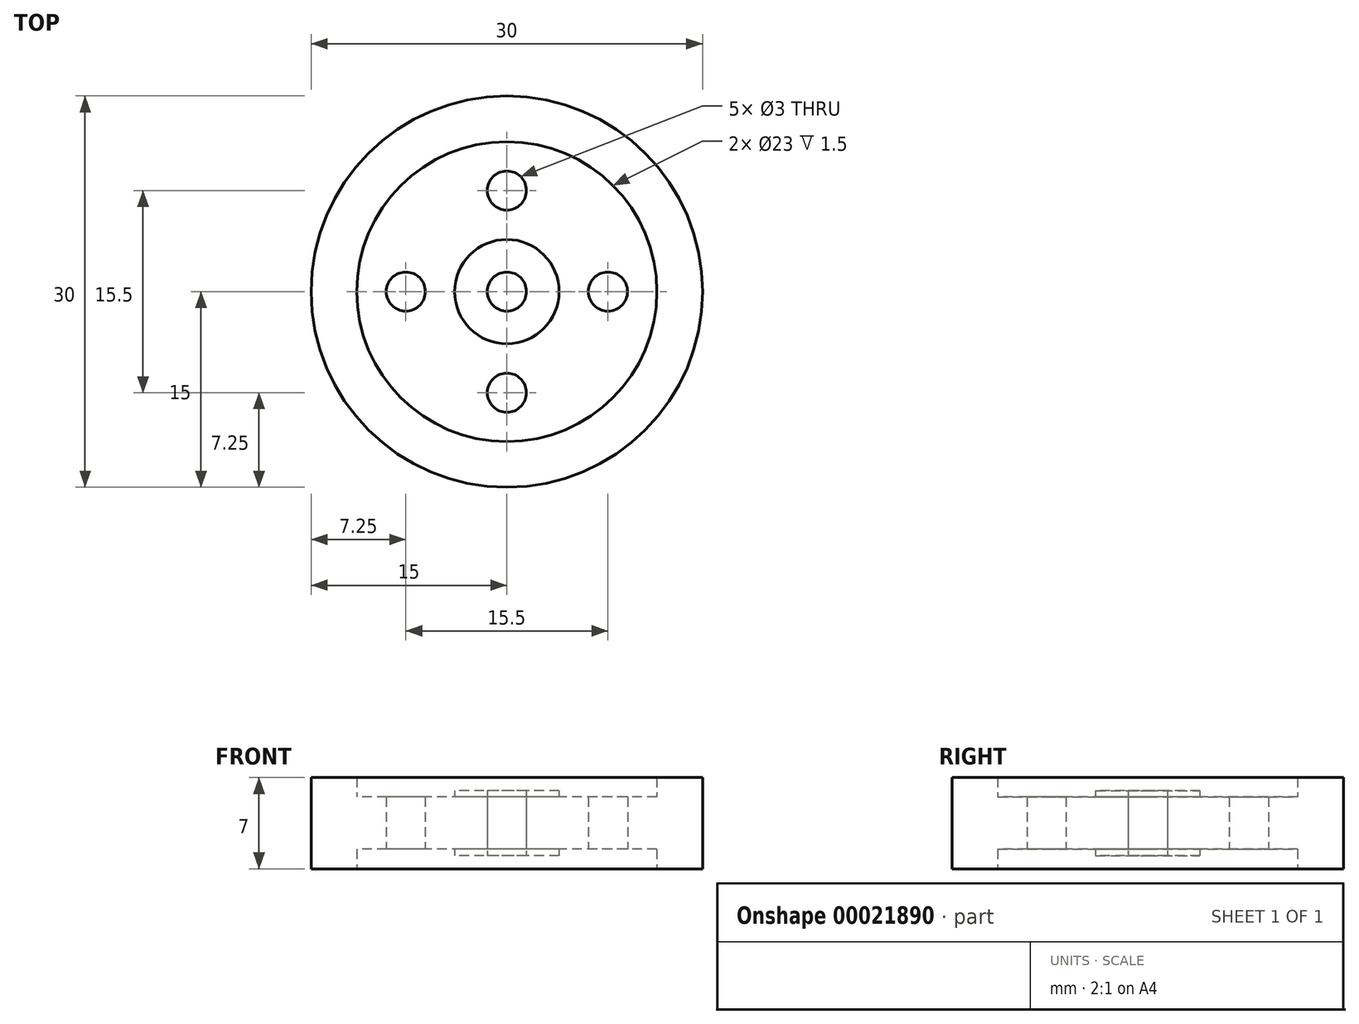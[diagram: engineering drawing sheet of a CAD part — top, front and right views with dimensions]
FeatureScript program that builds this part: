
annotation { "Feature Type Name" : "Feature", "Feature Type Description" : "" }
export const myFeature = defineFeature(function(context is Context, id is Id, definition is map)
    precondition{}
    {
        {
            var Q0;
            Q0=qCreatedBy(makeId("Top.planeOp"),FACE);
            var sketch = newSketch(context, id + "F0", { "sketchPlane" : qUnion([Q0])});
            skCircle(sketch, "E0", {"center": v(0, 0) * mm, "radius": 15 * mm});
            skCircle(sketch, "E1", {"center": v(0, 0) * mm, "radius": 11.5 * mm});
            skCircle(sketch, "E2", {"center": v(0, 0) * mm, "radius": 4 * mm});
            skCircle(sketch, "E3", {"center": v(0, 0) * mm, "radius": 1.5 * mm});
            skLineSegment(sketch, "E4", {"start": v(0, 4) * mm, "end": v(0, 11.5) * mm});
            skLineSegment(sketch, "E5", {"start": v(0, 4) * mm, "end": v(0, 7.75) * mm});
            skCircle(sketch, "E6", {"center": v(0, 7.75) * mm, "radius": 1.5 * mm});
            skCircle(sketch, "E7.1.0", {"center": v(-7.75, 0) * mm, "radius": 1.5 * mm});
            skCircle(sketch, "E7.2.0", {"center": v(0, -7.75) * mm, "radius": 1.5 * mm});
            skCircle(sketch, "E7.3.0", {"center": v(7.75, 0) * mm, "radius": 1.5 * mm});
            skSolve(sketch);
        }
        {
            var Q0;
            Q0=makeQuery(id+"F0.imprint","IMPRINT",FACE,{"disambiguationData":[TD([[makeQuery(id+"F0.imprint","IMPRINT",EDGE,{"derivedFrom":sQuery(id+"F0.wireOp",EDGE,"E0")}),1.0]])]});
            extrude(context, id + "F1", {"entities" : qUnion([Q0]), "endBound" : BoundingType.SYMMETRIC, "depth" : 7 * mm});
        }
        {
            var Q0;
            Q0=makeQuery(id+"F0.imprint","IMPRINT",FACE,{"disambiguationData":[TD([[makeQuery(id+"F0.imprint","IMPRINT",EDGE,{"derivedFrom":sQuery(id+"F0.wireOp",EDGE,"E1")}),1.0]])]});
            extrude(context, id + "F2", {"entities" : qUnion([Q0]), "operationType" : NewBodyOperationType.ADD, "endBound" : BoundingType.SYMMETRIC, "depth" : 4 * mm});
        }
        {
            var Q0;
            Q0=makeQuery(id+"F0.imprint","IMPRINT",FACE,{"disambiguationData":[TD([[makeQuery(id+"F0.imprint","IMPRINT",EDGE,{"derivedFrom":sQuery(id+"F0.wireOp",EDGE,"E2")}),1.0]])]});
            extrude(context, id + "F3", {"entities" : qUnion([Q0]), "operationType" : NewBodyOperationType.ADD, "endBound" : BoundingType.SYMMETRIC, "depth" : 5 * mm});
        }
    });
